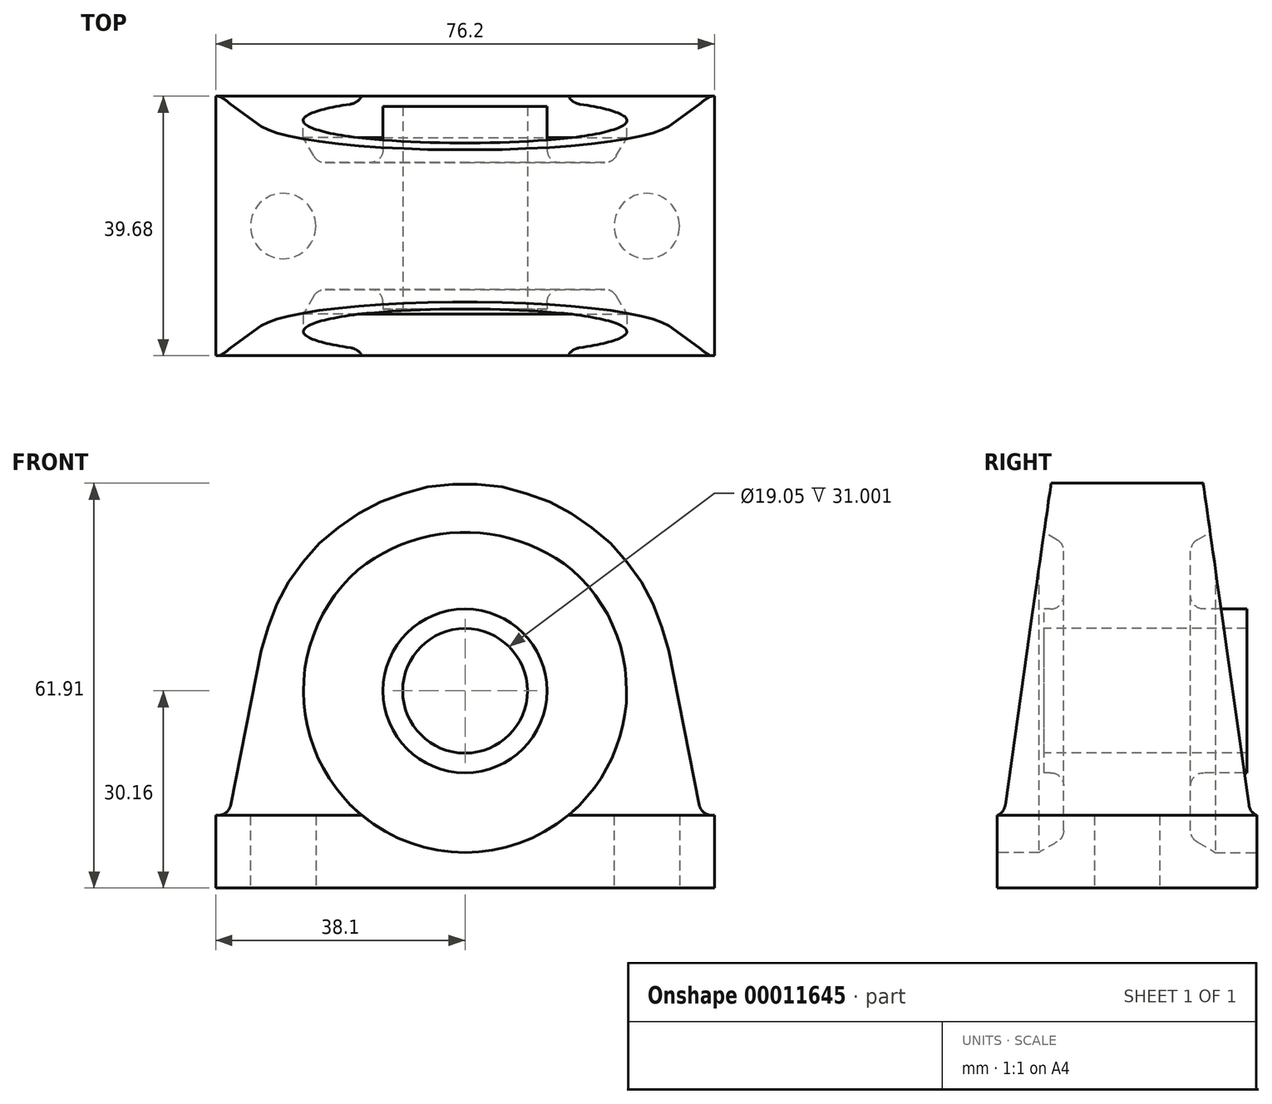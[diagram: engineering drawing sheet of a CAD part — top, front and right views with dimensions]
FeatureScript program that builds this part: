
annotation { "Feature Type Name" : "Feature", "Feature Type Description" : "" }
export const myFeature = defineFeature(function(context is Context, id is Id, definition is map)
    precondition{}
    {
        {
            var Q0;
            Q0=qCreatedBy(makeId("Right.planeOp"),FACE);
            var sketch = newSketch(context, id + "F0", { "sketchPlane" : qUnion([Q0])});
            skLineSegment(sketch, "E0", {"start": v(0, 0) * mm, "end": v(-37.76, 0) * mm, "construction": true});
            skLineSegment(sketch, "E1", {"start": v(0, 0) * mm, "end": v(41.3, 0) * mm, "construction": true});
            skLineSegment(sketch, "E2", {"start": v(0, 0) * mm, "end": v(0, 31.75) * mm, "construction": true});
            skLineSegment(sketch, "E3", {"start": v(0, 0) * mm, "end": v(0, -30.16) * mm, "construction": true});
            skLineSegment(sketch, "E4", {"start": v(-19.84, -30.16) * mm, "end": v(19.84, -30.16) * mm});
            skLineSegment(sketch, "E5", {"start": v(19.84, -30.16) * mm, "end": v(19.84, -19.05) * mm});
            skLineSegment(sketch, "E6", {"start": v(19.84, -19.05) * mm, "end": v(18.84, -19.05) * mm});
            skLineSegment(sketch, "E7", {"start": v(18.84, -19.05) * mm, "end": v(11.62, 31.75) * mm});
            skLineSegment(sketch, "E8", {"start": v(11.62, 31.75) * mm, "end": v(-11.62, 31.75) * mm});
            skLineSegment(sketch, "E9", {"start": v(-11.62, 31.75) * mm, "end": v(-18.84, -19.05) * mm});
            skLineSegment(sketch, "E10", {"start": v(-18.84, -19.05) * mm, "end": v(-19.84, -19.05) * mm});
            skLineSegment(sketch, "E11", {"start": v(-19.84, -19.05) * mm, "end": v(-19.84, -30.16) * mm});
            skLineSegment(sketch, "E12", {"start": v(-18.84, -19.05) * mm, "end": v(18.84, -19.05) * mm, "construction": true});
            skPoint(sketch, "E13", {"position": v(0, -19.05) * mm});
            skSolve(sketch);
        }
        {
            var Q0;
            Q0 = qSketchRegion(id + "F0", true);
            extrude(context, id + "F1", {"entities" : qUnion([Q0]), "endBound" : BoundingType.SYMMETRIC, "depth" : (25.4 * 3) * mm});
        }
        {
            var Q0;
            Q0=makeQuery(id+"F1.opExtrude","SWEPT_FACE",FACE,{"disambiguationData":[OSD([sQuery(id+"F0.wireOp",EDGE,"E11")])]});
            var sketch = newSketch(context, id + "F2", { "sketchPlane" : qUnion([Q0])});
            skArc(sketch, "E14", {"start": v(31.15, 6.12) * mm, "mid": v(0, 31.75) * mm, "end": v(-31.15, 6.12) * mm});
            skLineSegment(sketch, "E15", {"start": v(-31.15, 6.12) * mm, "end": v(-36.1, -19.05) * mm});
            skLineSegment(sketch, "E16", {"start": v(-36.1, -19.05) * mm, "end": v(-38.1, -19.05) * mm});
            skLineSegment(sketch, "E17", {"start": v(-38.1, -19.05) * mm, "end": v(-38.1, 36.75) * mm});
            skLineSegment(sketch, "E18", {"start": v(-38.1, 36.75) * mm, "end": v(38.1, 36.75) * mm});
            skLineSegment(sketch, "E19", {"start": v(38.1, 36.75) * mm, "end": v(38.1, -19.05) * mm});
            skLineSegment(sketch, "E20", {"start": v(38.1, -19.05) * mm, "end": v(36.1, -19.05) * mm});
            skLineSegment(sketch, "E21", {"start": v(36.1, -19.05) * mm, "end": v(31.15, 6.12) * mm});
            skLineSegment(sketch, "E22", {"start": v(-36.1, -19.05) * mm, "end": v(36.1, -19.05) * mm, "construction": true});
            skLineSegment(sketch, "E23", {"start": v(0, 0) * mm, "end": v(0, -19.05) * mm, "construction": true});
            skSolve(sketch);
        }
        {
            var Q0;
            Q0 = qSketchRegion(id + "F2", true);
            extrude(context, id + "F3", {"entities" : qUnion([Q0]), "operationType" : NewBodyOperationType.REMOVE, "endBound" : BoundingType.THROUGH_ALL, "oppositeDirection" : true, "depth" : 25 * mm});
        }
        {
            var Q0;
            Q0=qCreatedBy(makeId("Right.planeOp"),FACE);
            var sketch = newSketch(context, id + "F4", { "sketchPlane" : qUnion([Q0])});
            skLineSegment(sketch, "E24", {"start": v(0, 0) * mm, "end": v(-77.66, 0) * mm, "construction": true});
            skLineSegment(sketch, "E25", {"start": v(0, 0) * mm, "end": v(82.36, 0) * mm, "construction": true});
            skLineSegment(sketch, "E26", {"start": v(-50, 24.72) * mm, "end": v(-50, 0) * mm});
            skLineSegment(sketch, "E27", {"start": v(-50, 0) * mm, "end": v(50, 0) * mm});
            skLineSegment(sketch, "E28", {"start": v(50, 0) * mm, "end": v(50, 25) * mm});
            skLineSegment(sketch, "E29", {"start": v(13.5, 24.72) * mm, "end": v(10.7, 23.1) * mm});
            skLineSegment(sketch, "E30", {"start": v(9.7, 21.37) * mm, "end": v(9.7, 14.52) * mm});
            skLineSegment(sketch, "E31", {"start": v(11.7, 12.52) * mm, "end": v(18.3, 12.53) * mm});
            skLineSegment(sketch, "E32", {"start": v(18.3, 12.53) * mm, "end": v(18.3, 9.53) * mm});
            skLineSegment(sketch, "E33", {"start": v(18.3, 9.52) * mm, "end": v(-12.7, 9.52) * mm});
            skLineSegment(sketch, "E34", {"start": v(-12.7, 9.52) * mm, "end": v(-12.7, 12.53) * mm});
            skLineSegment(sketch, "E35", {"start": v(-12.7, 12.53) * mm, "end": v(-11.7, 12.53) * mm});
            skLineSegment(sketch, "E36", {"start": v(-9.7, 14.53) * mm, "end": v(-9.7, 21.37) * mm});
            skLineSegment(sketch, "E37", {"start": v(-10.7, 23.1) * mm, "end": v(-13.5, 24.72) * mm});
            skLineSegment(sketch, "E38", {"start": v(0, 0) * mm, "end": v(0, 55.47) * mm, "construction": true});
            skLineSegment(sketch, "E39", {"start": v(-9.7, 12.53) * mm, "end": v(9.7, 12.53) * mm, "construction": true});
            skLineSegment(sketch, "E40", {"start": v(-9.7, 22.52) * mm, "end": v(9.7, 22.52) * mm, "construction": true});
            skLineSegment(sketch, "E41", {"start": v(-13.5, 24.72) * mm, "end": v(13.5, 24.72) * mm, "construction": true});
            skPoint(sketch, "E42", {"position": v(0, 26) * mm});
            skPoint(sketch, "E43", {"position": v(0, 24.72) * mm});
            skPoint(sketch, "E44", {"position": v(0, 22.52) * mm});
            skPoint(sketch, "E45", {"position": v(0, 12.53) * mm});
            skPoint(sketch, "E46.visualSharp", {"position": v(-9.7, 22.52) * mm});
            skArc(sketch, "E46.filletArc", {"start": v(-9.7, 21.37) * mm, "mid": v(-9.97, 22.37) * mm, "end": v(-10.7, 23.1) * mm});
            skPoint(sketch, "E47.visualSharp", {"position": v(9.7, 22.53) * mm});
            skArc(sketch, "E47.filletArc", {"start": v(10.7, 23.1) * mm, "mid": v(9.97, 22.37) * mm, "end": v(9.7, 21.37) * mm});
            skPoint(sketch, "E48.visualSharp", {"position": v(9.7, 12.53) * mm});
            skArc(sketch, "E48.filletArc", {"start": v(9.7, 14.52) * mm, "mid": v(10.29, 13.11) * mm, "end": v(11.7, 12.52) * mm});
            skPoint(sketch, "E49.visualSharp", {"position": v(-9.7, 12.53) * mm});
            skArc(sketch, "E49.filletArc", {"start": v(-11.7, 12.53) * mm, "mid": v(-10.29, 13.11) * mm, "end": v(-9.7, 14.53) * mm});
            skLineSegment(sketch, "E50", {"start": v(13.5, 24.72) * mm, "end": v(50, 25) * mm});
            skLineSegment(sketch, "E51", {"start": v(-13.5, 24.72) * mm, "end": v(-50, 24.72) * mm});
            skSolve(sketch);
        }
        {
            var Q0;
            Q0=makeQuery(id+"F1.opExtrude","SWEPT_FACE",FACE,{"disambiguationData":[OSD([sQuery(id+"F0.wireOp",EDGE,"E5")])]});
            var sketch = newSketch(context, id + "F5", { "sketchPlane" : qUnion([Q0])});
            skCircle(sketch, "E52", {"center": v(0, 0) * mm, "radius": 15 * mm});
            skSolve(sketch);
        }
        {
            var Q0;
            Q0 = qSketchRegion(id + "F5", true);
            extrude(context, id + "F6", {"entities" : qUnion([Q0]), "operationType" : NewBodyOperationType.ADD, "depth" : 6.39 * mm, "hasSecondDirection" : true, "secondDirectionOppositeDirection" : true, "secondDirectionDepth" : 43.9 * mm});
        }
        {
            var Q0;
            Q0 = qSketchRegion(id + "F4", true);
            var Q1;
            Q1=sQuery(id+"F4.wireOp",EDGE,"E24");
            revolve(context, id + "F7", {"operationType" : NewBodyOperationType.REMOVE, "entities" : qUnion([Q0]), "axis" : qUnion([Q1]), "revolveType" : RevolveType.FULL, "oppositeDirection" : true});
        }
        {
            var Q0;
            {var subQ0=sQuery(id+"F0.wireOp",EDGE,"E9");var subQ1=sQuery(id+"F0.wireOp",EDGE,"E10");Q0=makeQuery(id+"F7.boolean.opBoolean","SPLIT",EDGE,{"disambiguationData":[TD([makeQuery(id+"F3.boolean.opBoolean","COPY",FACE,{"derivedFrom":makeQuery(id+"F3.opExtrude","SWEPT_FACE",FACE,{"disambiguationData":[OSD([sQuery(id+"F2.wireOp",EDGE,"E21")])]})})])],"derivedFrom":makeQuery(id+"F1.opExtrude","SWEPT_EDGE",EDGE,{"disambiguationData":[OSD([subQ0,subQ1])]})});}
            var Q1;
            Q1=makeQuery(id+"F3.boolean.opBoolean","COPY",EDGE,{"derivedFrom":makeQuery(id+"F3.opExtrude","SWEPT_EDGE",EDGE,{"disambiguationData":[OSD([sQuery(id+"F0.wireOp",EDGE,"E10"),sQuery(id+"F0.wireOp",EDGE,"E11"),sQuery(id+"F2.wireOp",EDGE,"E20"),sQuery(id+"F2.wireOp",EDGE,"E21")])]})});
            var Q2;
            {var subQ0=sQuery(id+"F0.wireOp",EDGE,"E6");var subQ1=sQuery(id+"F0.wireOp",EDGE,"E7");Q2=makeQuery(id+"F7.boolean.opBoolean","SPLIT",EDGE,{"disambiguationData":[TD([makeQuery(id+"F3.boolean.opBoolean","COPY",FACE,{"derivedFrom":makeQuery(id+"F3.opExtrude","SWEPT_FACE",FACE,{"disambiguationData":[OSD([sQuery(id+"F2.wireOp",EDGE,"E21")])]})})])],"derivedFrom":makeQuery(id+"F1.opExtrude","SWEPT_EDGE",EDGE,{"disambiguationData":[OSD([subQ0,subQ1])]})});}
            var Q3;
            {var subQ0=sQuery(id+"F0.wireOp",EDGE,"E6");var subQ1=sQuery(id+"F0.wireOp",EDGE,"E7");Q3=makeQuery(id+"F7.boolean.opBoolean","SPLIT",EDGE,{"disambiguationData":[TD([makeQuery(id+"F3.boolean.opBoolean","COPY",FACE,{"derivedFrom":makeQuery(id+"F3.opExtrude","SWEPT_FACE",FACE,{"disambiguationData":[OSD([sQuery(id+"F2.wireOp",EDGE,"E15")])]})})])],"derivedFrom":makeQuery(id+"F1.opExtrude","SWEPT_EDGE",EDGE,{"disambiguationData":[OSD([subQ0,subQ1])]})});}
            var Q4;
            Q4=makeQuery(id+"F3.boolean.opBoolean","COPY",EDGE,{"derivedFrom":makeQuery(id+"F3.opExtrude","SWEPT_EDGE",EDGE,{"disambiguationData":[OSD([sQuery(id+"F0.wireOp",EDGE,"E10"),sQuery(id+"F0.wireOp",EDGE,"E11"),sQuery(id+"F2.wireOp",EDGE,"E15"),sQuery(id+"F2.wireOp",EDGE,"E16")])]})});
            var Q5;
            {var subQ0=sQuery(id+"F0.wireOp",EDGE,"E9");var subQ1=sQuery(id+"F0.wireOp",EDGE,"E10");Q5=makeQuery(id+"F7.boolean.opBoolean","SPLIT",EDGE,{"disambiguationData":[TD([makeQuery(id+"F3.boolean.opBoolean","COPY",FACE,{"derivedFrom":makeQuery(id+"F3.opExtrude","SWEPT_FACE",FACE,{"disambiguationData":[OSD([sQuery(id+"F2.wireOp",EDGE,"E15")])]})})])],"derivedFrom":makeQuery(id+"F1.opExtrude","SWEPT_EDGE",EDGE,{"disambiguationData":[OSD([subQ0,subQ1])]})});}
            fillet(context, id + "F8", {"entities" : qUnion([Q0, Q1, Q2, Q3, Q4, Q5]), "radius" : 2 * mm, "tangentPropagation" : true, "allowEdgeOverflow" : false});
        }
        {
            var Q0;
            Q0=makeQuery(id+"F1.opExtrude","SWEPT_FACE",FACE,{"disambiguationData":[OSD([sQuery(id+"F0.wireOp",EDGE,"E4")])]});
            var sketch = newSketch(context, id + "F9", { "sketchPlane" : qUnion([Q0])});
            skLineSegment(sketch, "E53", {"start": v(0, -19.84) * mm, "end": v(0, 19.84) * mm, "construction": true});
            skLineSegment(sketch, "E54", {"start": v(27.78, 0) * mm, "end": v(-27.78, 0) * mm, "construction": true});
            skPoint(sketch, "E55", {"position": v(0, 0) * mm});
            skCircle(sketch, "E56", {"center": v(27.78, 0) * mm, "radius": 5 * mm});
            skCircle(sketch, "E57", {"center": v(-27.78, 0) * mm, "radius": 5 * mm});
            skSolve(sketch);
        }
        {
            var Q0;
            Q0 = qSketchRegion(id + "F9", true);
            extrude(context, id + "F10", {"entities" : qUnion([Q0]), "operationType" : NewBodyOperationType.REMOVE, "oppositeDirection" : true, "depth" : ((7 / 16) * 25.4) * mm});
        }
    });
